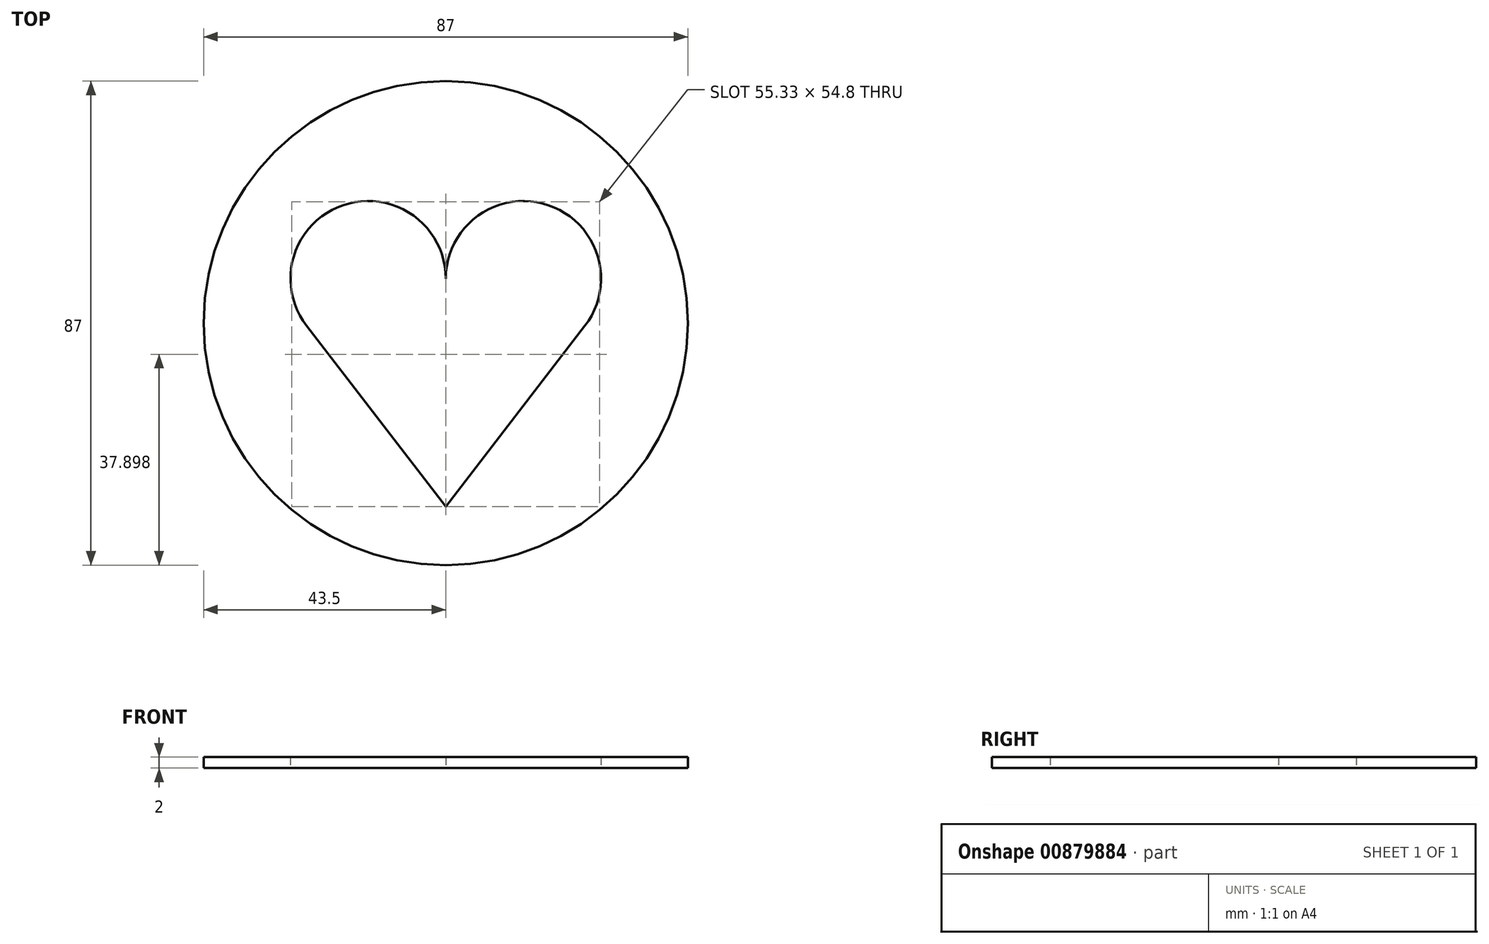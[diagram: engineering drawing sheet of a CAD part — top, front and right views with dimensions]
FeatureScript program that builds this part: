
annotation { "Feature Type Name" : "Feature", "Feature Type Description" : "" }
export const myFeature = defineFeature(function(context is Context, id is Id, definition is map)
    precondition{}
    {
        {
            var Q0;
            Q0=qCreatedBy(makeId("Top.planeOp"),FACE);
            var sketch = newSketch(context, id + "F0", { "sketchPlane" : qUnion([Q0])});
            skCircle(sketch, "E0", {"center": v(0, 0) * mm, "radius": 43.5 * mm});
            skLineSegment(sketch, "E1", {"start": v(-9.04, 0) * mm, "end": v(8.66, 0) * mm, "construction": true});
            skLineSegment(sketch, "E2", {"start": v(0, -6.64) * mm, "end": v(0, 6.77) * mm, "construction": true});
            skLineSegment(sketch, "E3", {"start": v(0, -33) * mm, "end": v(-25, -0.5) * mm});
            skLineSegment(sketch, "E4", {"start": v(0, -33) * mm, "end": v(25, -0.5) * mm});
            skLineSegment(sketch, "E5", {"start": v(0, 6.77) * mm, "end": v(0, 8) * mm});
            skArc(sketch, "E6", {"start": v(0, 8) * mm, "mid": v(-18.44, 21.2) * mm, "end": v(-25, -0.5) * mm});
            skArc(sketch, "E7", {"start": v(25, -0.5) * mm, "mid": v(18.44, 21.2) * mm, "end": v(0, 8) * mm});
            skSolve(sketch);
        }
        {
            var Q0;
            Q0=makeQuery(id+"F0.imprint","IMPRINT",FACE,{"disambiguationData":[TD([[makeQuery(id+"F0.imprint","IMPRINT",EDGE,{"derivedFrom":sQuery(id+"F0.wireOp",EDGE,"E0")}),1.0]])]});
            extrude(context, id + "F1", {"entities" : qUnion([Q0]), "depth" : 2 * mm, "offsetDistance" : 25 * mm});
        }
    });
